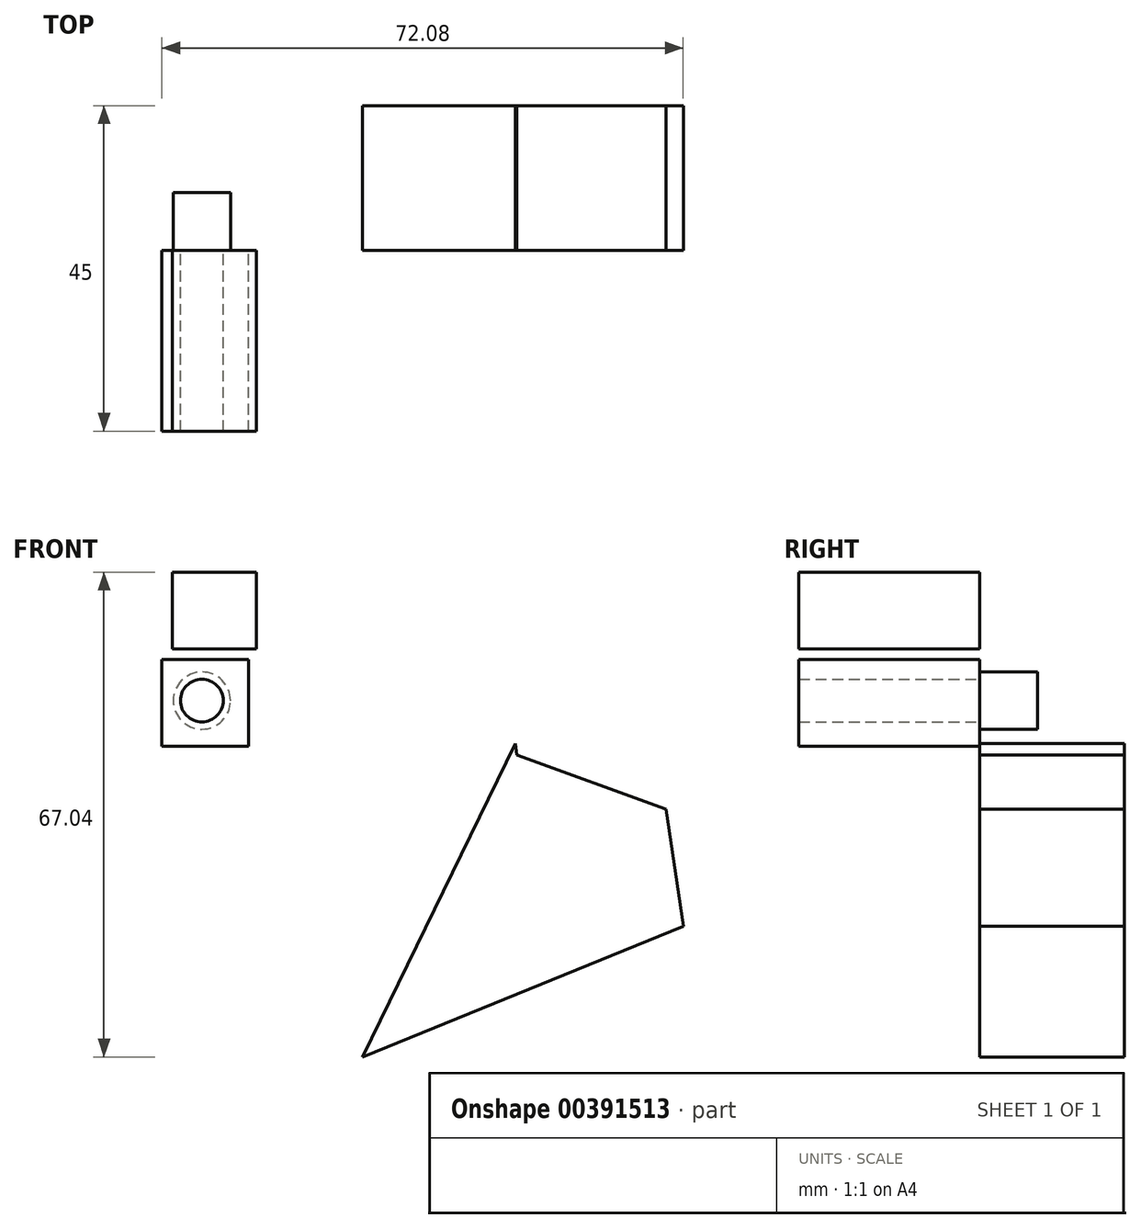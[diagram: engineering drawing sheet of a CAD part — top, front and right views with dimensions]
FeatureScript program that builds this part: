
annotation { "Feature Type Name" : "Feature", "Feature Type Description" : "" }
export const myFeature = defineFeature(function(context is Context, id is Id, definition is map)
    precondition{}
    {
        {
            var Q0;
            Q0=qCreatedBy(makeId("Front.planeOp"),FACE);
            var sketch = newSketch(context, id + "F0", { "sketchPlane" : qUnion([Q0])});
            skLineSegment(sketch, "E0", {"start": v(21.13, 43.34) * mm, "end": v(0, 0) * mm});
            skLineSegment(sketch, "E1", {"start": v(0, 0) * mm, "end": v(44.36, 18.09) * mm});
            skLineSegment(sketch, "E2", {"start": v(44.36, 18.09) * mm, "end": v(42, 34.23) * mm});
            skLineSegment(sketch, "E3", {"start": v(42, 34.23) * mm, "end": v(21.36, 41.74) * mm});
            skLineSegment(sketch, "E4", {"start": v(21.36, 41.74) * mm, "end": v(21.13, 43.34) * mm});
            skLineSegment(sketch, "E5", {"start": v(26.85, 137.76) * mm, "end": v(26.85, 137.76) * mm});
            skSolve(sketch);
        }
        {
            var Q0;
            Q0=makeQuery(id+"F0.imprint","IMPRINT",FACE,{"disambiguationData":[TD([[makeQuery(id+"F0.imprint","IMPRINT",EDGE,{"derivedFrom":sQuery(id+"F0.wireOp",EDGE,"E0")}),1.0]])]});
            var Q1;
            Q1 = qSketchRegion(id + "F0", true);
            extrude(context, id + "F1", {"entities" : qUnion([Q0, Q1]), "oppositeDirection" : true, "depth" : 20 * mm});
        }
        {
            var Q0;
            Q0=qCreatedBy(makeId("Front.planeOp"),FACE);
            var sketch = newSketch(context, id + "F2", { "sketchPlane" : qUnion([Q0])});
            skLineSegment(sketch, "E6.bottom", {"start": v(-27.72, 54.96) * mm, "end": v(-15.73, 54.96) * mm});
            skLineSegment(sketch, "E6.top", {"start": v(-27.72, 42.97) * mm, "end": v(-15.73, 42.97) * mm});
            skLineSegment(sketch, "E6.left", {"start": v(-27.72, 54.96) * mm, "end": v(-27.72, 42.97) * mm});
            skLineSegment(sketch, "E6.right", {"start": v(-15.73, 54.96) * mm, "end": v(-15.73, 42.97) * mm});
            skLineSegment(sketch, "E7", {"start": v(-15.92, 34.75) * mm, "end": v(-35.92, 34.52) * mm});
            skCircle(sketch, "E8", {"center": v(-22.2, 49.28) * mm, "radius": 2.95 * mm});
            skSolve(sketch);
        }
        {
            var Q0;
            Q0=makeQuery(id+"F2.imprint","IMPRINT",FACE,{"disambiguationData":[TD([[makeQuery(id+"F2.imprint","IMPRINT",EDGE,{"derivedFrom":sQuery(id+"F2.wireOp",EDGE,"E8")}),1.0]])]});
            var sketch = newSketch(context, id + "F3", { "sketchPlane" : qUnion([Q0])});
            skPoint(sketch, "E9.0.3.start.orphan", {"position": v(-15.73, 54.96) * mm});
            skPoint(sketch, "E9.0.0.start.orphan", {"position": v(-27.72, 54.96) * mm});
            skPoint(sketch, "E9.0.1.end.orphan", {"position": v(-15.73, 42.97) * mm});
            skPoint(sketch, "E9.0.1.start.orphan", {"position": v(-27.72, 42.97) * mm});
            skLineSegment(sketch, "E10.0.0", {"start": v(0, 0) * mm, "end": v(21.13, 43.34) * mm});
            skLineSegment(sketch, "E10.0.2", {"start": v(21.13, 43.34) * mm, "end": v(0, 0) * mm});
            skLineSegment(sketch, "E10.1.0", {"start": v(21.36, 41.74) * mm, "end": v(42, 34.23) * mm});
            skLineSegment(sketch, "E10.1.2", {"start": v(42, 34.23) * mm, "end": v(21.36, 41.74) * mm});
            skCircle(sketch, "E11.0", {"center": v(-22.2, 49.28) * mm, "radius": 2.95 * mm});
            skLineSegment(sketch, "E12.0.0", {"start": v(-27.72, 54.96) * mm, "end": v(-27.72, 42.97) * mm});
            skLineSegment(sketch, "E12.0.1", {"start": v(-27.72, 42.97) * mm, "end": v(-15.73, 42.97) * mm});
            skLineSegment(sketch, "E12.0.2", {"start": v(-15.73, 42.97) * mm, "end": v(-15.73, 54.96) * mm});
            skLineSegment(sketch, "E12.0.3", {"start": v(-15.73, 54.96) * mm, "end": v(-27.72, 54.96) * mm});
            skSolve(sketch);
        }
        {
            var Q0;
            Q0 = qSketchRegion(id + "F3", true);
            extrude(context, id + "F4", {"entities" : qUnion([Q0]), "depth" : 25 * mm});
        }
        {
            var Q0;
            Q0=makeQuery(id+"F2.imprint","IMPRINT",FACE,{"disambiguationData":[TD([[makeQuery(id+"F2.imprint","IMPRINT",EDGE,{"derivedFrom":sQuery(id+"F2.wireOp",EDGE,"E8")}),1.0]])]});
            var sketch = newSketch(context, id + "F5", { "sketchPlane" : qUnion([Q0])});
            skCircle(sketch, "E13.0", {"center": v(-22.2, 49.28) * mm, "radius": 3.95 * mm});
            skSolve(sketch);
        }
        {
            var Q0;
            Q0 = qSketchRegion(id + "F5", true);
            extrude(context, id + "F6", {"entities" : qUnion([Q0]), "operationType" : NewBodyOperationType.ADD, "oppositeDirection" : true, "depth" : 8 * mm});
        }
        {
            var Q0;
            Q0=sQuery(id+"F2.wireOp",EDGE,"E8");
            extrude(context, id + "F7", {"bodyType" : ToolBodyType.SURFACE, "surfaceEntities" : qUnion([Q0]), "oppositeDirection" : true, "depth" : 15.46 * mm});
        }
        {
            var Q0;
            Q0=qCreatedBy(makeId("Front.planeOp"),FACE);
            var sketch = newSketch(context, id + "F8", { "sketchPlane" : qUnion([Q0])});
            skLineSegment(sketch, "E14.bottom", {"start": v(-26.3, 67.04) * mm, "end": v(-14.67, 67.04) * mm});
            skLineSegment(sketch, "E14.top", {"start": v(-26.3, 56.42) * mm, "end": v(-14.67, 56.42) * mm});
            skLineSegment(sketch, "E14.left", {"start": v(-26.3, 67.04) * mm, "end": v(-26.3, 56.42) * mm});
            skLineSegment(sketch, "E14.right", {"start": v(-14.67, 67.04) * mm, "end": v(-14.67, 56.42) * mm});
            skCircle(sketch, "E15", {"center": v(-14.67, 67.04) * mm, "radius": 5.85 * mm});
            skSolve(sketch);
        }
        {
            var Q0;
            {var subQ0=sQuery(id+"F8.wireOp",EDGE,"E14.right");var subQ1=sQuery(id+"F8.wireOp",EDGE,"E14.bottom");var subQ2=makeQuery(id+"F8.imprint","INTERSECT",VERTEX,{"derivedFrom":[subQ1,subQ0]});Q0=makeQuery(id+"F8.imprint","IMPRINT",FACE,{"disambiguationData":[TD([[makeQuery(id+"F8.imprint","IMPRINT",EDGE,{"disambiguationData":[TD([[subQ2,1.0]])],"derivedFrom":subQ1}),-1.0]])]});}
            var Q1;
            {var subQ1=sQuery(id+"F8.wireOp",EDGE,"E14.top");Q1=makeQuery(id+"F8.imprint","IMPRINT",FACE,{"disambiguationData":[TD([[makeQuery(id+"F8.imprint","IMPRINT",EDGE,{"derivedFrom":subQ1}),1.0]])]});}
            extrude(context, id + "F9", {"entities" : qUnion([Q0, Q1]), "depth" : 25 * mm});
        }
    });
